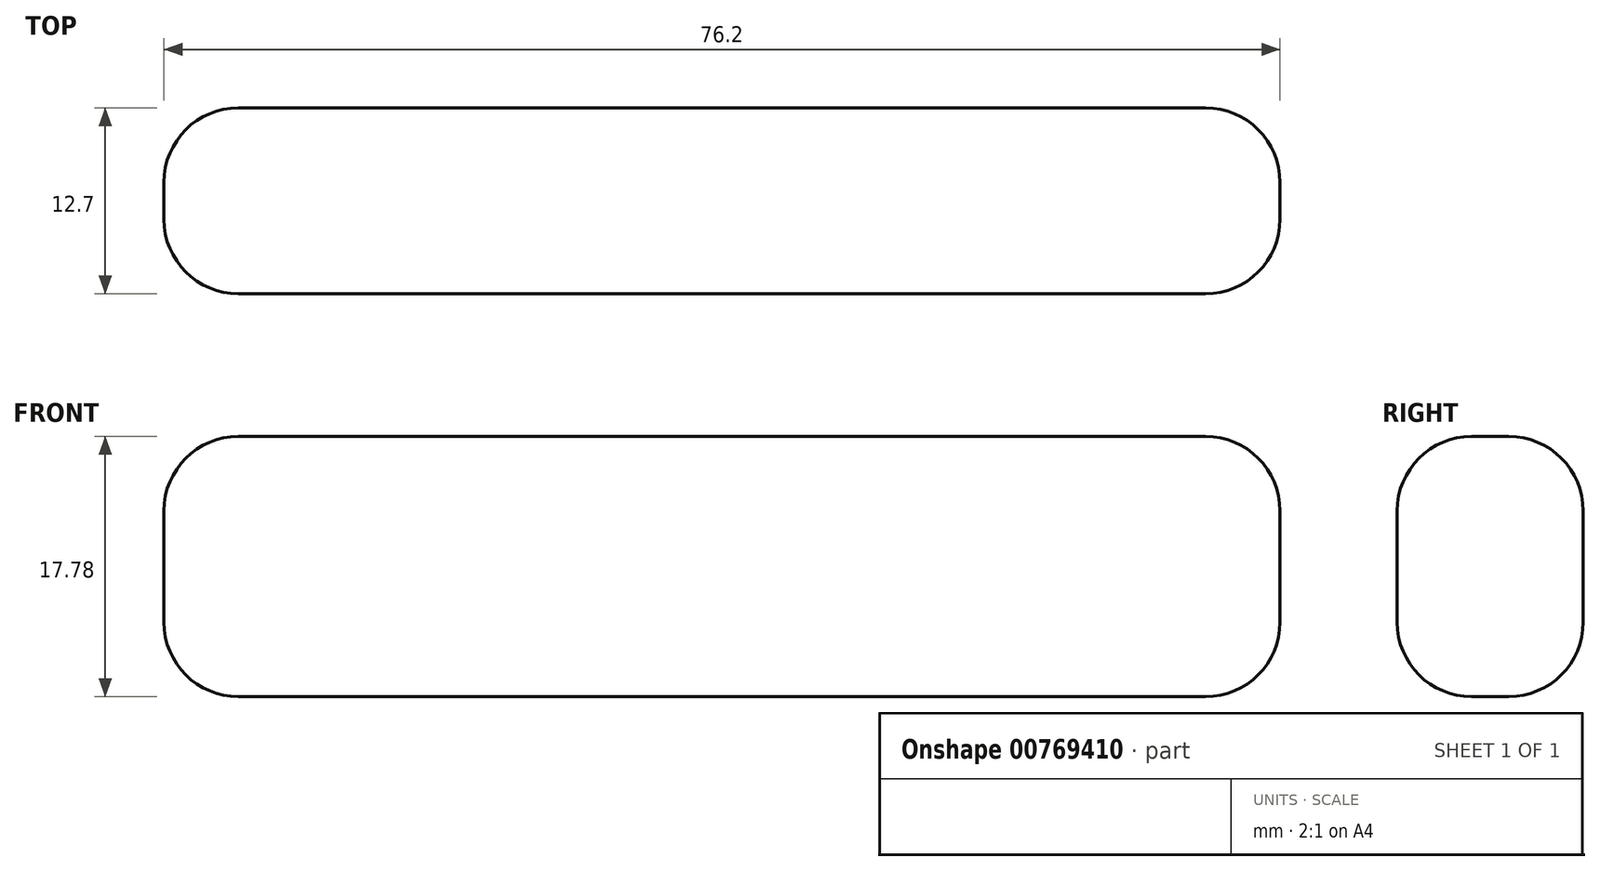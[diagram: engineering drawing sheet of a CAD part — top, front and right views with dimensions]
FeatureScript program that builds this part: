
annotation { "Feature Type Name" : "Feature", "Feature Type Description" : "" }
export const myFeature = defineFeature(function(context is Context, id is Id, definition is map)
    precondition{}
    {
        {
            var Q0;
            Q0=qCreatedBy(makeId("Top.planeOp"),FACE);
            var sketch = newSketch(context, id + "F0", { "sketchPlane" : qUnion([Q0])});
            skLineSegment(sketch, "E0.bottom", {"start": v(38.1, -6.35) * mm, "end": v(-38.1, -6.35) * mm});
            skLineSegment(sketch, "E0.top", {"start": v(38.1, 6.35) * mm, "end": v(-38.1, 6.35) * mm});
            skLineSegment(sketch, "E0.left", {"start": v(38.1, -6.35) * mm, "end": v(38.1, 6.35) * mm});
            skLineSegment(sketch, "E0.right", {"start": v(-38.1, -6.35) * mm, "end": v(-38.1, 6.35) * mm});
            skPoint(sketch, "E0.middle", {"position": v(0, 0) * mm});
            skSolve(sketch);
        }
        {
            var Q0;
            Q0=makeQuery(id+"F0.imprint","IMPRINT",FACE,{"disambiguationData":[TD([[makeQuery(id+"F0.imprint","IMPRINT",EDGE,{"derivedFrom":sQuery(id+"F0.wireOp",EDGE,"E0.bottom")}),-1.0]])]});
            extrude(context, id + "F1", {"entities" : qUnion([Q0]), "depth" : 17.78 * mm, "offsetDistance" : 25.4 * mm});
        }
        {
            var Q0;
            Q0=makeQuery(id+"F1.opExtrude","CAP_EDGE",EDGE,{"disambiguationData":[OSD([sQuery(id+"F0.wireOp",EDGE,"E0.top")])],"isStart":false});
            var Q1;
            Q1=makeQuery(id+"F1.opExtrude","CAP_EDGE",EDGE,{"disambiguationData":[OSD([sQuery(id+"F0.wireOp",EDGE,"E0.bottom")])],"isStart":false});
            var Q2;
            Q2=makeQuery(id+"F1.opExtrude","CAP_EDGE",EDGE,{"disambiguationData":[OSD([sQuery(id+"F0.wireOp",EDGE,"E0.top")])],"isStart":true});
            var Q3;
            Q3=makeQuery(id+"F1.opExtrude","CAP_EDGE",EDGE,{"disambiguationData":[OSD([sQuery(id+"F0.wireOp",EDGE,"E0.bottom")])],"isStart":true});
            fillet(context, id + "F2", {"entities" : qUnion([Q0, Q1, Q2, Q3]), "radius" : 5.08 * mm, "tangentPropagation" : true, "allowEdgeOverflow" : false});
        }
        {
            var Q0;
            Q0=makeQuery(id+"F1.opExtrude","CAP_EDGE",EDGE,{"disambiguationData":[OSD([sQuery(id+"F0.wireOp",EDGE,"E0.right")])],"isStart":false});
            var Q1;
            Q1=makeQuery(id+"F2.opFillet","BLEND_EDGE",EDGE,{"blendedFrom":[makeQuery(id+"F1.opExtrude","CAP_EDGE",EDGE,{"disambiguationData":[OSD([sQuery(id+"F0.wireOp",EDGE,"E0.bottom")])],"isStart":false}),makeQuery(id+"F1.opExtrude","SWEPT_FACE",FACE,{"disambiguationData":[OSD([sQuery(id+"F0.wireOp",EDGE,"E0.right")])]})],"blendedInto":[makeQuery(id+"F1.opExtrude","SWEPT_FACE",FACE,{"disambiguationData":[OSD([sQuery(id+"F0.wireOp",EDGE,"E0.right")])]})]});
            var Q2;
            Q2=makeQuery(id+"F2.opFillet","BLEND_EDGE",EDGE,{"blendedFrom":[makeQuery(id+"F1.opExtrude","CAP_EDGE",EDGE,{"disambiguationData":[OSD([sQuery(id+"F0.wireOp",EDGE,"E0.top")])],"isStart":false}),makeQuery(id+"F1.opExtrude","SWEPT_FACE",FACE,{"disambiguationData":[OSD([sQuery(id+"F0.wireOp",EDGE,"E0.right")])]})],"blendedInto":[makeQuery(id+"F1.opExtrude","SWEPT_FACE",FACE,{"disambiguationData":[OSD([sQuery(id+"F0.wireOp",EDGE,"E0.right")])]})]});
            var Q3;
            Q3=makeQuery(id+"F1.opExtrude","SWEPT_EDGE",EDGE,{"disambiguationData":[OSD([sQuery(id+"F0.wireOp",EDGE,"E0.top"),sQuery(id+"F0.wireOp",EDGE,"E0.right")])]});
            var Q4;
            Q4=makeQuery(id+"F1.opExtrude","SWEPT_EDGE",EDGE,{"disambiguationData":[OSD([sQuery(id+"F0.wireOp",EDGE,"E0.bottom"),sQuery(id+"F0.wireOp",EDGE,"E0.right")])]});
            var Q5;
            Q5=makeQuery(id+"F2.opFillet","BLEND_EDGE",EDGE,{"blendedFrom":[makeQuery(id+"F1.opExtrude","CAP_EDGE",EDGE,{"disambiguationData":[OSD([sQuery(id+"F0.wireOp",EDGE,"E0.bottom")])],"isStart":true}),makeQuery(id+"F1.opExtrude","SWEPT_FACE",FACE,{"disambiguationData":[OSD([sQuery(id+"F0.wireOp",EDGE,"E0.right")])]})],"blendedInto":[makeQuery(id+"F1.opExtrude","SWEPT_FACE",FACE,{"disambiguationData":[OSD([sQuery(id+"F0.wireOp",EDGE,"E0.right")])]})]});
            var Q6;
            Q6=makeQuery(id+"F1.opExtrude","CAP_EDGE",EDGE,{"disambiguationData":[OSD([sQuery(id+"F0.wireOp",EDGE,"E0.right")])],"isStart":true});
            var Q7;
            Q7=makeQuery(id+"F2.opFillet","BLEND_EDGE",EDGE,{"blendedFrom":[makeQuery(id+"F1.opExtrude","CAP_EDGE",EDGE,{"disambiguationData":[OSD([sQuery(id+"F0.wireOp",EDGE,"E0.top")])],"isStart":true}),makeQuery(id+"F1.opExtrude","SWEPT_FACE",FACE,{"disambiguationData":[OSD([sQuery(id+"F0.wireOp",EDGE,"E0.right")])]})],"blendedInto":[makeQuery(id+"F1.opExtrude","SWEPT_FACE",FACE,{"disambiguationData":[OSD([sQuery(id+"F0.wireOp",EDGE,"E0.right")])]})]});
            fillet(context, id + "F3", {"entities" : qUnion([Q0, Q1, Q2, Q3, Q4, Q5, Q6, Q7]), "radius" : 5.08 * mm, "tangentPropagation" : true, "allowEdgeOverflow" : false});
        }
        {
            var Q0;
            Q0=makeQuery(id+"F2.opFillet","BLEND_EDGE",EDGE,{"blendedFrom":[makeQuery(id+"F1.opExtrude","CAP_EDGE",EDGE,{"disambiguationData":[OSD([sQuery(id+"F0.wireOp",EDGE,"E0.bottom")])],"isStart":false}),makeQuery(id+"F1.opExtrude","SWEPT_FACE",FACE,{"disambiguationData":[OSD([sQuery(id+"F0.wireOp",EDGE,"E0.left")])]})],"blendedInto":[makeQuery(id+"F1.opExtrude","SWEPT_FACE",FACE,{"disambiguationData":[OSD([sQuery(id+"F0.wireOp",EDGE,"E0.left")])]})]});
            var Q1;
            Q1=makeQuery(id+"F1.opExtrude","CAP_EDGE",EDGE,{"disambiguationData":[OSD([sQuery(id+"F0.wireOp",EDGE,"E0.left")])],"isStart":false});
            var Q2;
            Q2=makeQuery(id+"F2.opFillet","BLEND_EDGE",EDGE,{"blendedFrom":[makeQuery(id+"F1.opExtrude","CAP_EDGE",EDGE,{"disambiguationData":[OSD([sQuery(id+"F0.wireOp",EDGE,"E0.top")])],"isStart":false}),makeQuery(id+"F1.opExtrude","SWEPT_FACE",FACE,{"disambiguationData":[OSD([sQuery(id+"F0.wireOp",EDGE,"E0.left")])]})],"blendedInto":[makeQuery(id+"F1.opExtrude","SWEPT_FACE",FACE,{"disambiguationData":[OSD([sQuery(id+"F0.wireOp",EDGE,"E0.left")])]})]});
            var Q3;
            Q3=makeQuery(id+"F1.opExtrude","SWEPT_EDGE",EDGE,{"disambiguationData":[OSD([sQuery(id+"F0.wireOp",EDGE,"E0.top"),sQuery(id+"F0.wireOp",EDGE,"E0.left")])]});
            var Q4;
            Q4=makeQuery(id+"F2.opFillet","BLEND_EDGE",EDGE,{"blendedFrom":[makeQuery(id+"F1.opExtrude","CAP_EDGE",EDGE,{"disambiguationData":[OSD([sQuery(id+"F0.wireOp",EDGE,"E0.top")])],"isStart":true}),makeQuery(id+"F1.opExtrude","SWEPT_FACE",FACE,{"disambiguationData":[OSD([sQuery(id+"F0.wireOp",EDGE,"E0.left")])]})],"blendedInto":[makeQuery(id+"F1.opExtrude","SWEPT_FACE",FACE,{"disambiguationData":[OSD([sQuery(id+"F0.wireOp",EDGE,"E0.left")])]})]});
            var Q5;
            Q5=makeQuery(id+"F1.opExtrude","CAP_EDGE",EDGE,{"disambiguationData":[OSD([sQuery(id+"F0.wireOp",EDGE,"E0.left")])],"isStart":true});
            var Q6;
            Q6=makeQuery(id+"F2.opFillet","BLEND_EDGE",EDGE,{"blendedFrom":[makeQuery(id+"F1.opExtrude","CAP_EDGE",EDGE,{"disambiguationData":[OSD([sQuery(id+"F0.wireOp",EDGE,"E0.bottom")])],"isStart":true}),makeQuery(id+"F1.opExtrude","SWEPT_FACE",FACE,{"disambiguationData":[OSD([sQuery(id+"F0.wireOp",EDGE,"E0.left")])]})],"blendedInto":[makeQuery(id+"F1.opExtrude","SWEPT_FACE",FACE,{"disambiguationData":[OSD([sQuery(id+"F0.wireOp",EDGE,"E0.left")])]})]});
            var Q7;
            Q7=makeQuery(id+"F1.opExtrude","SWEPT_EDGE",EDGE,{"disambiguationData":[OSD([sQuery(id+"F0.wireOp",EDGE,"E0.bottom"),sQuery(id+"F0.wireOp",EDGE,"E0.left")])]});
            fillet(context, id + "F4", {"entities" : qUnion([Q0, Q1, Q2, Q3, Q4, Q5, Q6, Q7]), "radius" : 5.08 * mm, "tangentPropagation" : true, "allowEdgeOverflow" : false});
        }
    });
